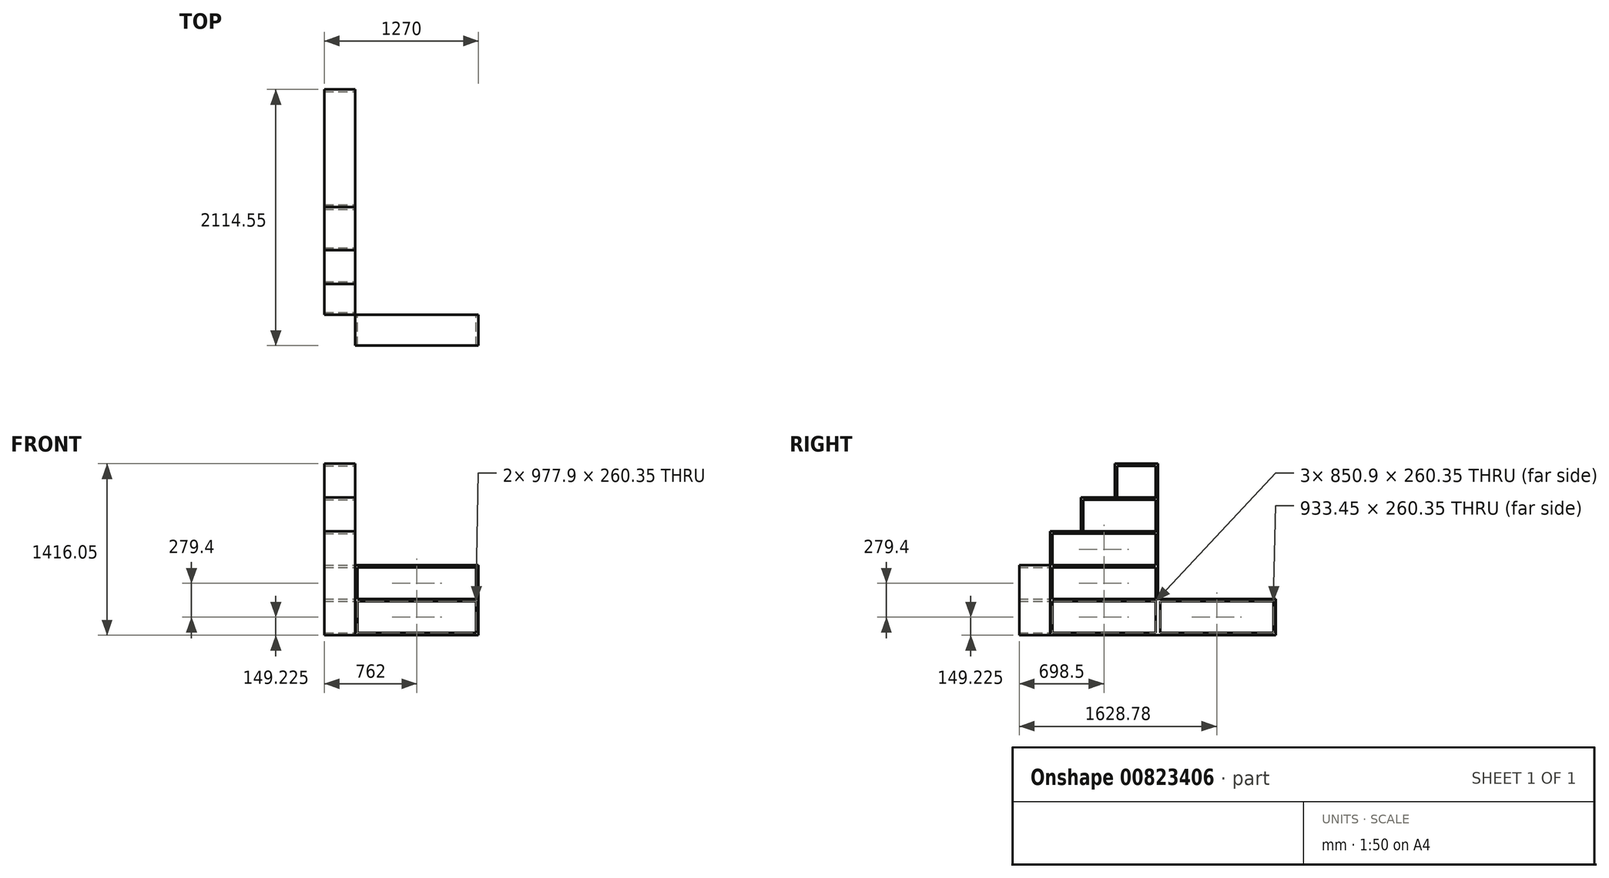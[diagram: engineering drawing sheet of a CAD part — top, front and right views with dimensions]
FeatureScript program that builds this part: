
annotation { "Feature Type Name" : "Feature", "Feature Type Description" : "" }
export const myFeature = defineFeature(function(context is Context, id is Id, definition is map)
    precondition{}
    {
        {
            var Q0;
            Q0=qCreatedBy(makeId("Front.planeOp"),FACE);
            var sketch = newSketch(context, id + "F0", { "sketchPlane" : qUnion([Q0])});
            skLineSegment(sketch, "E0.bottom", {"start": v(0, 0) * mm, "end": v(1016, 0) * mm});
            skLineSegment(sketch, "E0.top", {"start": v(0, 577.85) * mm, "end": v(1016, 577.85) * mm});
            skLineSegment(sketch, "E0.left", {"start": v(0, 0) * mm, "end": v(0, 577.85) * mm});
            skLineSegment(sketch, "E0.right", {"start": v(1016, 0) * mm, "end": v(1016, 577.85) * mm});
            skLineSegment(sketch, "E1.bottom", {"start": v(19.05, 558.8) * mm, "end": v(996.95, 558.8) * mm});
            skLineSegment(sketch, "E1.top", {"start": v(19.05, 298.45) * mm, "end": v(996.95, 298.45) * mm});
            skLineSegment(sketch, "E1.left", {"start": v(19.05, 558.8) * mm, "end": v(19.05, 298.45) * mm});
            skLineSegment(sketch, "E1.right", {"start": v(996.95, 558.8) * mm, "end": v(996.95, 298.45) * mm});
            skLineSegment(sketch, "E2.bottom", {"start": v(19.05, 279.4) * mm, "end": v(996.95, 279.4) * mm});
            skLineSegment(sketch, "E2.top", {"start": v(19.05, 19.05) * mm, "end": v(996.95, 19.05) * mm});
            skLineSegment(sketch, "E2.left", {"start": v(19.05, 279.4) * mm, "end": v(19.05, 19.05) * mm});
            skLineSegment(sketch, "E2.right", {"start": v(996.95, 279.4) * mm, "end": v(996.95, 19.05) * mm});
            skSolve(sketch);
        }
        {
            var Q0;
            Q0 = qSketchRegion(id + "F0", true);
            extrude(context, id + "F1", {"entities" : qUnion([Q0]), "depth" : 254 * mm, "offsetDistance" : 25.4 * mm});
        }
        {
            var Q0;
            Q0=makeQuery(id+"F1.opExtrude","SWEPT_FACE",FACE,{"disambiguationData":[OSD([sQuery(id+"F0.wireOp",EDGE,"E0.left")])]});
            var sketch = newSketch(context, id + "F2", { "sketchPlane" : qUnion([Q0])});
            skLineSegment(sketch, "E3.bottom", {"start": v(0, 857.25) * mm, "end": v(-889, 857.25) * mm});
            skLineSegment(sketch, "E3.top", {"start": v(0, 0) * mm, "end": v(-889, 0) * mm});
            skLineSegment(sketch, "E3.left", {"start": v(0, 857.25) * mm, "end": v(0, 0) * mm});
            skLineSegment(sketch, "E3.right", {"start": v(-889, 857.25) * mm, "end": v(-889, 0) * mm});
            skPoint(sketch, "E4.oppositeSnap0", {"position": v(-889, 428.63) * mm});
            skLineSegment(sketch, "E5.top", {"start": v(-869.95, 19.05) * mm, "end": v(-19.05, 19.05) * mm});
            skLineSegment(sketch, "E5.left", {"start": v(-869.95, 279.4) * mm, "end": v(-869.95, 19.05) * mm});
            skLineSegment(sketch, "E5.right", {"start": v(-19.05, 279.4) * mm, "end": v(-19.05, 19.05) * mm});
            skLineSegment(sketch, "E6", {"start": v(-19.05, 279.4) * mm, "end": v(-869.95, 279.4) * mm});
            skLineSegment(sketch, "E7.bottom", {"start": v(-19.05, 298.45) * mm, "end": v(-869.95, 298.45) * mm});
            skLineSegment(sketch, "E7.top", {"start": v(-19.05, 558.8) * mm, "end": v(-869.95, 558.8) * mm});
            skLineSegment(sketch, "E7.left", {"start": v(-19.05, 298.45) * mm, "end": v(-19.05, 558.8) * mm});
            skLineSegment(sketch, "E7.right", {"start": v(-869.95, 298.45) * mm, "end": v(-869.95, 558.8) * mm});
            skLineSegment(sketch, "E8.bottom", {"start": v(-19.05, 577.85) * mm, "end": v(-869.95, 577.85) * mm});
            skLineSegment(sketch, "E8.top", {"start": v(-19.05, 838.2) * mm, "end": v(-869.95, 838.2) * mm});
            skLineSegment(sketch, "E8.left", {"start": v(-19.05, 577.85) * mm, "end": v(-19.05, 838.2) * mm});
            skLineSegment(sketch, "E8.right", {"start": v(-869.95, 577.85) * mm, "end": v(-869.95, 838.2) * mm});
            skSolve(sketch);
        }
        {
            var Q0;
            Q0 = qSketchRegion(id + "F2", true);
            extrude(context, id + "F3", {"entities" : qUnion([Q0]), "depth" : 254 * mm, "offsetDistance" : 25.4 * mm});
        }
        {
            var Q0;
            Q0=makeQuery(id+"F3.opExtrude","CAP_FACE",FACE,{"disambiguationData":[OSD([sQuery(id+"F2.wireOp",EDGE,"E3.bottom"),sQuery(id+"F2.wireOp",EDGE,"E3.top"),sQuery(id+"F2.wireOp",EDGE,"E3.left"),sQuery(id+"F2.wireOp",EDGE,"E3.right"),sQuery(id+"F2.wireOp",EDGE,"E4.bottom"),sQuery(id+"F2.wireOp",EDGE,"E4.top"),sQuery(id+"F2.wireOp",EDGE,"E4.left"),sQuery(id+"F2.wireOp",EDGE,"E4.right"),sQuery(id+"F2.wireOp",EDGE,"E5.bottom"),sQuery(id+"F2.wireOp",EDGE,"E5.top"),sQuery(id+"F2.wireOp",EDGE,"E5.left"),sQuery(id+"F2.wireOp",EDGE,"E5.right")])],"isStart":false});
            var sketch = newSketch(context, id + "F4", { "sketchPlane" : qUnion([Q0])});
            skLineSegment(sketch, "E9.MirrorCS", {"start": v(-958.85, 628.65) * mm, "end": v(-920.75, 628.65) * mm, "construction": true});
            skLineSegment(sketch, "E10.MirrorCS", {"start": v(-1695.45, 628.65) * mm, "end": v(-1733.55, 628.65) * mm, "construction": true});
            skLineSegment(sketch, "E11.MirrorCS", {"start": v(279.4, 835.02) * mm, "end": v(-920.75, 2006.6) * mm, "construction": true});
            skLineSegment(sketch, "E12.MirrorCS", {"start": v(-920.75, 520.7) * mm, "end": v(-1733.55, 520.7) * mm, "construction": true});
            skLineSegment(sketch, "E13.MirrorCS", {"start": v(-1733.55, 520.7) * mm, "end": v(-1733.55, 628.65) * mm, "construction": true});
            skLineSegment(sketch, "E14.MirrorCS", {"start": v(-1695.45, 628.65) * mm, "end": v(-1695.45, 1790.7) * mm, "construction": true});
            skLineSegment(sketch, "E15.MirrorCS", {"start": v(-920.75, 628.65) * mm, "end": v(-920.75, 520.7) * mm, "construction": true});
            skLineSegment(sketch, "E16.MirrorCS", {"start": v(-958.85, 1790.7) * mm, "end": v(-958.85, 628.65) * mm, "construction": true});
            skLineSegment(sketch, "E17.MirrorCS", {"start": v(-1695.45, 1790.7) * mm, "end": v(-958.85, 1790.7) * mm, "construction": true});
            skLineSegment(sketch, "E18", {"start": v(-1911.35, 0) * mm, "end": v(-1911.35, 2374.9) * mm, "construction": true});
            skLineSegment(sketch, "E19", {"start": v(-920.75, 2006.6) * mm, "end": v(-1298.03, 2374.9) * mm, "construction": true});
            skLineSegment(sketch, "E20", {"start": v(-1911.35, 2374.9) * mm, "end": v(-1298.03, 2374.9) * mm, "construction": true});
            skSolve(sketch);
        }
        {
            var Q0;
            Q0=makeQuery(id+"F3.opExtrude","CAP_FACE",FACE,{"disambiguationData":[OSD([sQuery(id+"F2.wireOp",EDGE,"E3.bottom"),sQuery(id+"F2.wireOp",EDGE,"E3.top"),sQuery(id+"F2.wireOp",EDGE,"E3.left"),sQuery(id+"F2.wireOp",EDGE,"E3.right"),sQuery(id+"F2.wireOp",EDGE,"E5.top"),sQuery(id+"F2.wireOp",EDGE,"E5.left"),sQuery(id+"F2.wireOp",EDGE,"E5.right"),sQuery(id+"F2.wireOp",EDGE,"E6"),sQuery(id+"F2.wireOp",EDGE,"E7.bottom"),sQuery(id+"F2.wireOp",EDGE,"E7.top"),sQuery(id+"F2.wireOp",EDGE,"E7.left"),sQuery(id+"F2.wireOp",EDGE,"E7.right"),sQuery(id+"F2.wireOp",EDGE,"E8.bottom"),sQuery(id+"F2.wireOp",EDGE,"E8.top"),sQuery(id+"F2.wireOp",EDGE,"E8.left"),sQuery(id+"F2.wireOp",EDGE,"E8.right")])],"isStart":true});
            var sketch = newSketch(context, id + "F5", { "sketchPlane" : qUnion([Q0])});
            skLineSegment(sketch, "E21.top", {"start": v(889, 1136.65) * mm, "end": v(254, 1136.65) * mm});
            skLineSegment(sketch, "E21.left", {"start": v(889, 857.25) * mm, "end": v(889, 1136.65) * mm});
            skLineSegment(sketch, "E21.right", {"start": v(254, 857.25) * mm, "end": v(254, 1136.65) * mm});
            skLineSegment(sketch, "E22.bottom", {"start": v(273.05, 1117.6) * mm, "end": v(869.95, 1117.6) * mm});
            skLineSegment(sketch, "E22.left", {"start": v(273.05, 1117.6) * mm, "end": v(273.05, 857.25) * mm});
            skLineSegment(sketch, "E22.right", {"start": v(869.95, 1117.6) * mm, "end": v(869.95, 857.25) * mm});
            skLineSegment(sketch, "E23", {"start": v(254, 857.25) * mm, "end": v(273.05, 857.25) * mm});
            skLineSegment(sketch, "E24", {"start": v(869.95, 857.25) * mm, "end": v(889, 857.25) * mm});
            skSolve(sketch);
        }
        {
            var Q0;
            Q0 = qSketchRegion(id + "F5", true);
            extrude(context, id + "F6", {"entities" : qUnion([Q0]), "oppositeDirection" : true, "depth" : 254 * mm, "offsetDistance" : 25.4 * mm});
        }
        {
            var Q0;
            Q0=makeQuery(id+"F6.opExtrude","CAP_FACE",FACE,{"disambiguationData":[OSD([sQuery(id+"F5.wireOp",EDGE,"E21.top"),sQuery(id+"F5.wireOp",EDGE,"E21.left"),sQuery(id+"F5.wireOp",EDGE,"E21.right"),sQuery(id+"F5.wireOp",EDGE,"E22.bottom"),sQuery(id+"F5.wireOp",EDGE,"E22.left"),sQuery(id+"F5.wireOp",EDGE,"E22.right"),sQuery(id+"F5.wireOp",EDGE,"E23"),sQuery(id+"F5.wireOp",EDGE,"E24")])],"isStart":true});
            var sketch = newSketch(context, id + "F7", { "sketchPlane" : qUnion([Q0])});
            skLineSegment(sketch, "E25", {"start": v(533.4, 1136.65) * mm, "end": v(533.4, 1416.05) * mm});
            skLineSegment(sketch, "E26", {"start": v(533.4, 1416.05) * mm, "end": v(889, 1416.05) * mm});
            skLineSegment(sketch, "E27", {"start": v(889, 1416.05) * mm, "end": v(889, 1136.65) * mm});
            skLineSegment(sketch, "E28", {"start": v(889, 1136.65) * mm, "end": v(869.95, 1136.65) * mm});
            skLineSegment(sketch, "E29", {"start": v(869.95, 1136.65) * mm, "end": v(869.95, 1397) * mm});
            skLineSegment(sketch, "E30", {"start": v(869.95, 1397) * mm, "end": v(552.45, 1397) * mm});
            skLineSegment(sketch, "E31", {"start": v(552.45, 1397) * mm, "end": v(552.45, 1136.65) * mm});
            skLineSegment(sketch, "E32", {"start": v(552.45, 1136.65) * mm, "end": v(533.4, 1136.65) * mm});
            skSolve(sketch);
        }
        {
            var Q0;
            Q0=makeQuery(id+"F7.imprint","IMPRINT",FACE,{"disambiguationData":[TD([[makeQuery(id+"F7.imprint","IMPRINT",EDGE,{"derivedFrom":sQuery(id+"F7.wireOp",EDGE,"E25")}),-1.0]])]});
            extrude(context, id + "F8", {"entities" : qUnion([Q0]), "oppositeDirection" : true, "depth" : 254 * mm, "offsetDistance" : 25.4 * mm});
        }
        {
            var Q0;
            Q0=makeQuery(id+"F3.opExtrude","CAP_FACE",FACE,{"disambiguationData":[OSD([sQuery(id+"F2.wireOp",EDGE,"E3.bottom"),sQuery(id+"F2.wireOp",EDGE,"E3.top"),sQuery(id+"F2.wireOp",EDGE,"E3.left"),sQuery(id+"F2.wireOp",EDGE,"E3.right"),sQuery(id+"F2.wireOp",EDGE,"E5.top"),sQuery(id+"F2.wireOp",EDGE,"E5.left"),sQuery(id+"F2.wireOp",EDGE,"E5.right"),sQuery(id+"F2.wireOp",EDGE,"E6"),sQuery(id+"F2.wireOp",EDGE,"E7.bottom"),sQuery(id+"F2.wireOp",EDGE,"E7.top"),sQuery(id+"F2.wireOp",EDGE,"E7.left"),sQuery(id+"F2.wireOp",EDGE,"E7.right"),sQuery(id+"F2.wireOp",EDGE,"E8.bottom"),sQuery(id+"F2.wireOp",EDGE,"E8.top"),sQuery(id+"F2.wireOp",EDGE,"E8.left"),sQuery(id+"F2.wireOp",EDGE,"E8.right")])],"isStart":true});
            var sketch = newSketch(context, id + "F9", { "sketchPlane" : qUnion([Q0])});
            skLineSegment(sketch, "E33.bottom", {"start": v(889, 0) * mm, "end": v(1860.55, 0) * mm});
            skLineSegment(sketch, "E33.top", {"start": v(889, 298.45) * mm, "end": v(1860.55, 298.45) * mm});
            skLineSegment(sketch, "E33.left", {"start": v(889, 0) * mm, "end": v(889, 298.45) * mm});
            skLineSegment(sketch, "E33.right", {"start": v(1860.55, 0) * mm, "end": v(1860.55, 298.45) * mm});
            skLineSegment(sketch, "E34.bottom", {"start": v(908.05, 279.4) * mm, "end": v(1841.5, 279.4) * mm});
            skLineSegment(sketch, "E34.top", {"start": v(908.05, 19.05) * mm, "end": v(1841.5, 19.05) * mm});
            skLineSegment(sketch, "E34.left", {"start": v(908.05, 279.4) * mm, "end": v(908.05, 19.05) * mm});
            skLineSegment(sketch, "E34.right", {"start": v(1841.5, 279.4) * mm, "end": v(1841.5, 19.05) * mm});
            skSolve(sketch);
        }
        {
            var Q0;
            Q0 = qSketchRegion(id + "F9", true);
            extrude(context, id + "F10", {"entities" : qUnion([Q0]), "operationType" : NewBodyOperationType.ADD, "oppositeDirection" : true, "depth" : 254 * mm, "offsetDistance" : 25.4 * mm});
        }
    });
